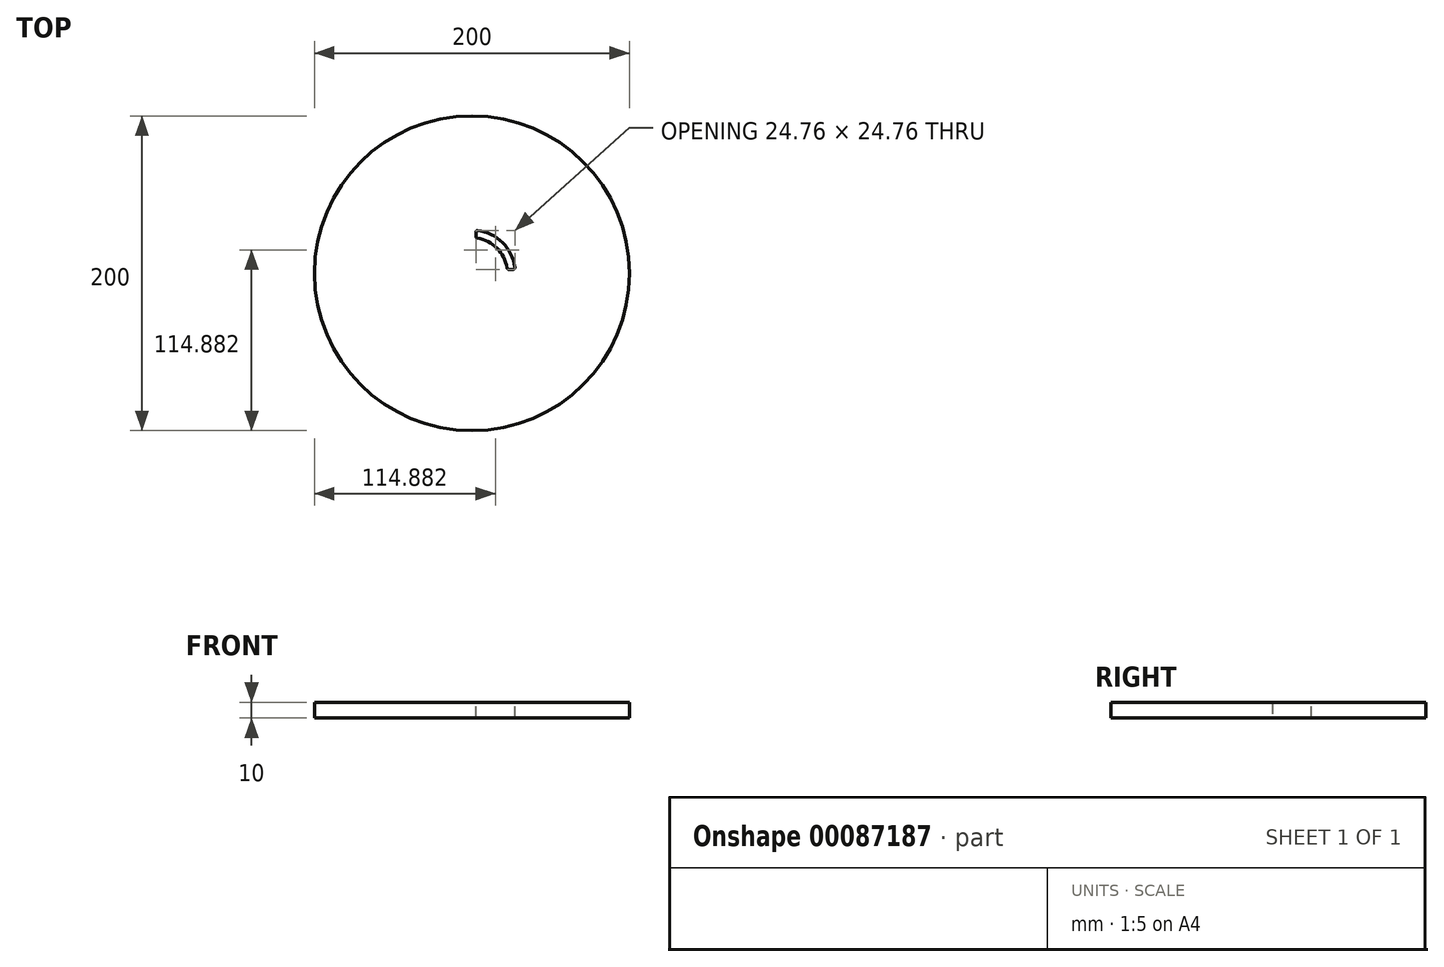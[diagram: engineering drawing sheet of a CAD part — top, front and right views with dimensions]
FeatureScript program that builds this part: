
annotation { "Feature Type Name" : "Feature", "Feature Type Description" : "" }
export const myFeature = defineFeature(function(context is Context, id is Id, definition is map)
    precondition{}
    {
        {
            var Q0;
            Q0=qCreatedBy(makeId("Top.planeOp"),FACE);
            var sketch = newSketch(context, id + "F0", { "sketchPlane" : qUnion([Q0])});
            skCircle(sketch, "E0", {"center": v(0, 0) * mm, "radius": 100 * mm});
            skSolve(sketch);
        }
        {
            var Q0;
            Q0=qSketchRegion(id+"F0",true);
            extrude(context, id + "F1", {"entities" : qUnion([Q0]), "depth" : 10 * mm});
        }
        {
            assignVariable(context, id + "F2", {"name" : "Diam", "anyValue" : 15});
        }
        {
            assignVariable(context, id + "F3", {"name" : "Diam", "anyValue" : getVariable(context, 'Diam') + 30});
        }
        {
            assignVariable(context, id + "F4", {"name" : "Slots", "anyValue" : 0});
        }
        {
            assignVariable(context, id + "F5", {"name" : "Slots", "anyValue" : getVariable(context, 'Slots') + 4});
        }
        {
            var Q0;
            Q0=makeQuery(id+"F1.opExtrude","CAP_FACE",FACE,{"disambiguationData":[OSD([sQuery(id+"F0.wireOp",EDGE,"E0")])],"isStart":false});
            var sketch = newSketch(context, id + "F6", { "sketchPlane" : qUnion([Q0])});
            skLineSegment(sketch, "E1", {"start": v(0, 27.3) * mm, "end": v(0, 0) * mm, "construction": true});
            skArc(sketch, "E2", {"start": v(2.5, 27.39) * mm, "mid": v(19.45, 19.45) * mm, "end": v(27.39, 2.5) * mm});
            skArc(sketch, "E3", {"start": v(2.5, 22.36) * mm, "mid": v(15.9, 15.9) * mm, "end": v(22.36, 2.5) * mm});
            skLineSegment(sketch, "E4", {"start": v(2.5, 27.39) * mm, "end": v(2.5, 22.36) * mm});
            skLineSegment(sketch, "E5", {"start": v(22.36, 2.5) * mm, "end": v(27.39, 2.5) * mm});
            skLineSegment(sketch, "E6", {"start": v(0, 0) * mm, "end": v(30.23, 0) * mm, "construction": true});
            skSolve(sketch);
        }
        {
            var Q0;
            Q0=qSketchRegion(id+"F6",true);
            extrude(context, id + "F7", {"entities" : qUnion([Q0]), "operationType" : NewBodyOperationType.REMOVE, "endBound" : BoundingType.THROUGH_ALL, "oppositeDirection" : true, "depth" : 25 * mm});
        }
        {
            var Q0;
            Q0=makeQuery(id+"F7.boolean.opBoolean","COPY",EDGE,{"derivedFrom":makeQuery(id+"F7.opExtrude","SWEPT_EDGE",EDGE,{"disambiguationData":[OSD([sQuery(id+"F6.wireOp",EDGE,"E2"),sQuery(id+"F6.wireOp",EDGE,"E4")])]})});
            var Q1;
            Q1=makeQuery(id+"F7.boolean.opBoolean","COPY",EDGE,{"derivedFrom":makeQuery(id+"F7.opExtrude","SWEPT_EDGE",EDGE,{"disambiguationData":[OSD([sQuery(id+"F6.wireOp",EDGE,"E3"),sQuery(id+"F6.wireOp",EDGE,"E4")])]})});
            var Q2;
            Q2=makeQuery(id+"F7.boolean.opBoolean","COPY",EDGE,{"derivedFrom":makeQuery(id+"F7.opExtrude","SWEPT_EDGE",EDGE,{"disambiguationData":[OSD([sQuery(id+"F6.wireOp",EDGE,"E3"),sQuery(id+"F6.wireOp",EDGE,"E5")])]})});
            var Q3;
            Q3=makeQuery(id+"F7.boolean.opBoolean","COPY",EDGE,{"derivedFrom":makeQuery(id+"F7.opExtrude","SWEPT_EDGE",EDGE,{"disambiguationData":[OSD([sQuery(id+"F6.wireOp",EDGE,"E2"),sQuery(id+"F6.wireOp",EDGE,"E5")])]})});
            var Q4;
            Q4=makeQuery(id+"F7.boolean.opBoolean","COPY",EDGE,{"derivedFrom":makeQuery(id+"F7.opExtrude","CAP_EDGE",EDGE,{"disambiguationData":[OSD([sQuery(id+"F6.wireOp",EDGE,"E3")])],"isStart":true})});
            fillet(context, id + "F8", {"entities" : qUnion([Q0, Q1, Q2, Q3, Q4]), "radius" : 1 * mm, "tangentPropagation" : true, "allowEdgeOverflow" : false});
        }
    });
